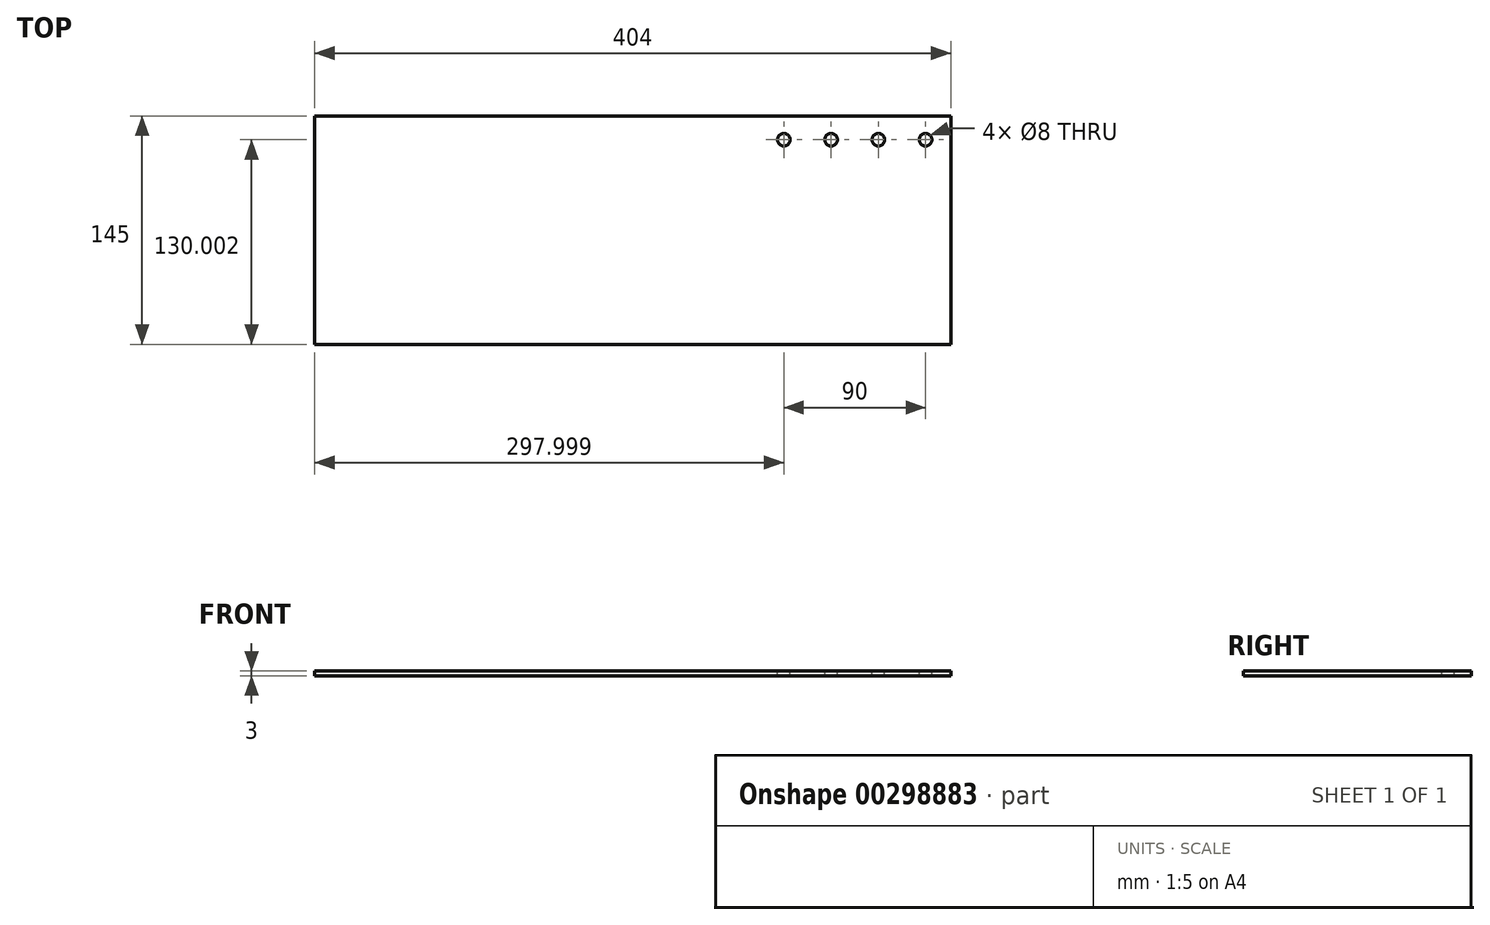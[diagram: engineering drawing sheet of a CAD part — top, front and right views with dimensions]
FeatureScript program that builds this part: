
annotation { "Feature Type Name" : "Feature", "Feature Type Description" : "" }
export const myFeature = defineFeature(function(context is Context, id is Id, definition is map)
    precondition{}
    {
        {
            var Q0;
            Q0=qCreatedBy(makeId("Top.planeOp"),FACE);
            var sketch = newSketch(context, id + "F0", { "sketchPlane" : qUnion([Q0])});
            skLineSegment(sketch, "E0.bottom", {"start": v(-204.41, 78.3) * mm, "end": v(199.59, 78.3) * mm});
            skLineSegment(sketch, "E0.top", {"start": v(-204.41, -66.7) * mm, "end": v(199.59, -66.7) * mm});
            skLineSegment(sketch, "E0.left", {"start": v(-204.41, 78.3) * mm, "end": v(-204.41, -66.7) * mm});
            skLineSegment(sketch, "E0.right", {"start": v(199.59, 78.3) * mm, "end": v(199.59, -66.7) * mm});
            skCircle(sketch, "E1", {"center": v(93.59, 63.3) * mm, "radius": 4 * mm});
            skCircle(sketch, "E2.1.0.0", {"center": v(123.59, 63.3) * mm, "radius": 4 * mm});
            skCircle(sketch, "E2.2.0.0", {"center": v(153.59, 63.3) * mm, "radius": 4 * mm});
            skCircle(sketch, "E2.3.0.0", {"center": v(183.59, 63.3) * mm, "radius": 4 * mm});
            skLineSegment(sketch, "E2.direction1", {"start": v(93.59, 63.3) * mm, "end": v(123.59, 63.3) * mm, "construction": true});
            skLineSegment(sketch, "E3", {"start": v(-199.41, 43.3) * mm, "end": v(-29.41, 43.3) * mm, "construction": true});
            skLineSegment(sketch, "E4", {"start": v(-29.41, 43.3) * mm, "end": v(-29.41, -66.7) * mm, "construction": true});
            skLineSegment(sketch, "E5", {"start": v(-29.41, -66.7) * mm, "end": v(-199.41, -66.7) * mm, "construction": true});
            skLineSegment(sketch, "E6", {"start": v(-199.41, -66.7) * mm, "end": v(-199.41, 43.3) * mm, "construction": true});
            skSolve(sketch);
        }
        {
            var Q0;
            Q0=makeQuery(id+"F0.imprint","IMPRINT",FACE,{"disambiguationData":[TD([[makeQuery(id+"F0.imprint","IMPRINT",EDGE,{"derivedFrom":sQuery(id+"F0.wireOp",EDGE,"E0.bottom")}),-1.0]])]});
            extrude(context, id + "F1", {"entities" : qUnion([Q0]), "oppositeDirection" : true, "depth" : 3 * mm});
        }
    });
